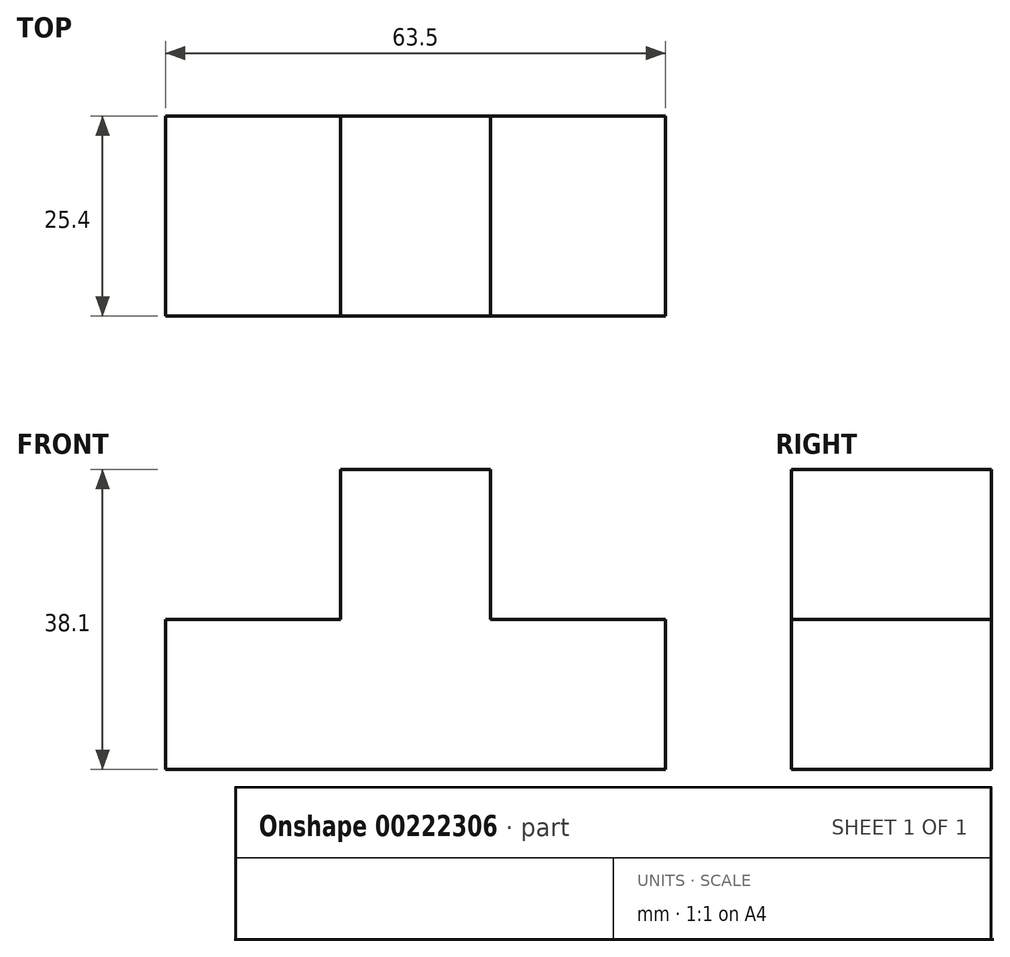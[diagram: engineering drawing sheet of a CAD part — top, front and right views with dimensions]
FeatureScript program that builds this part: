
annotation { "Feature Type Name" : "Feature", "Feature Type Description" : "" }
export const myFeature = defineFeature(function(context is Context, id is Id, definition is map)
    precondition{}
    {
        {
            var Q0;
            Q0=qCreatedBy(makeId("Front.planeOp"),FACE);
            var sketch = newSketch(context, id + "F0", { "sketchPlane" : qUnion([Q0])});
            skLineSegment(sketch, "E0.bottom", {"start": v(-41.28, 16.62) * mm, "end": v(22.23, 16.62) * mm});
            skLineSegment(sketch, "E0.top", {"start": v(-41.28, 35.67) * mm, "end": v(22.23, 35.67) * mm});
            skLineSegment(sketch, "E0.left", {"start": v(-41.28, 16.62) * mm, "end": v(-41.28, 35.67) * mm});
            skLineSegment(sketch, "E0.right", {"start": v(22.22, 16.62) * mm, "end": v(22.22, 35.67) * mm});
            skPoint(sketch, "E0.middle", {"position": v(-9.53, 26.14) * mm});
            skLineSegment(sketch, "E1.bottom", {"start": v(0, 35.67) * mm, "end": v(-19.05, 35.67) * mm});
            skLineSegment(sketch, "E1.top", {"start": v(0, 54.72) * mm, "end": v(-19.05, 54.72) * mm});
            skLineSegment(sketch, "E1.left", {"start": v(0, 35.67) * mm, "end": v(0, 54.72) * mm});
            skLineSegment(sketch, "E1.right", {"start": v(-19.05, 35.67) * mm, "end": v(-19.05, 54.72) * mm});
            skPoint(sketch, "E1.middle", {"position": v(-9.53, 45.2) * mm});
            skPoint(sketch, "E1.middle.positionSnap0", {"position": v(-9.53, 35.67) * mm});
            skPoint(sketch, "E1.centerSnap0", {"position": v(-9.53, 35.67) * mm});
            skSolve(sketch);
        }
        {
            var Q0;
            Q0 = qSketchRegion(id + "F0", true);
            extrude(context, id + "F1", {"entities" : qUnion([Q0]), "endBound" : BoundingType.SYMMETRIC, "depth" : 25.4 * mm});
        }
    });
